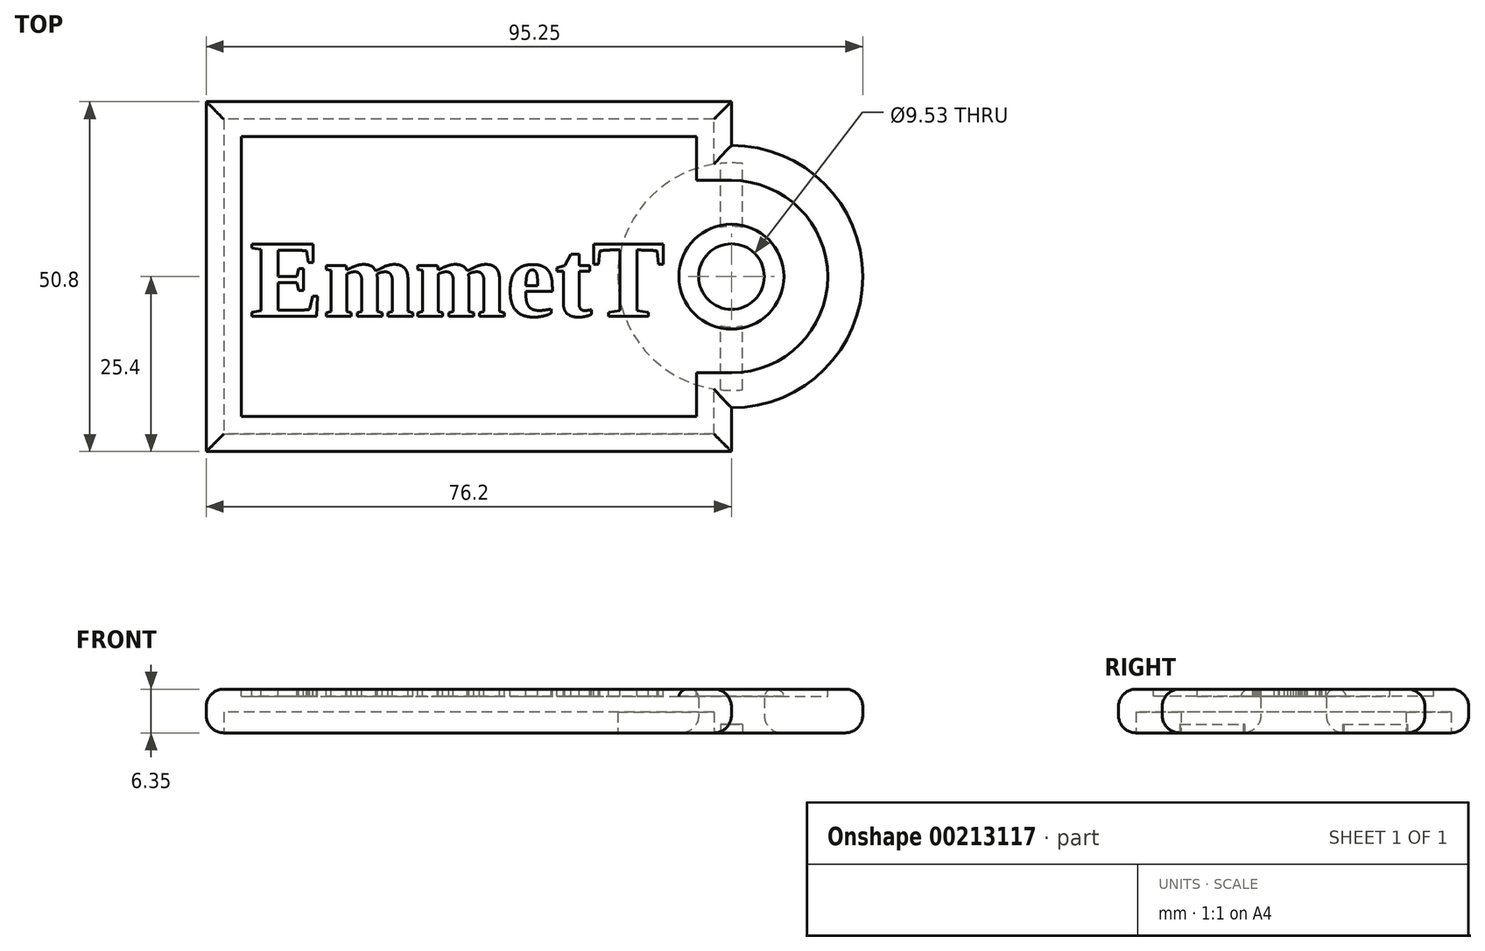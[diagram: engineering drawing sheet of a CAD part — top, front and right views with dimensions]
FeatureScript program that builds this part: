
annotation { "Feature Type Name" : "Feature", "Feature Type Description" : "" }
export const myFeature = defineFeature(function(context is Context, id is Id, definition is map)
    precondition{}
    {
        {
            var Q0;
            Q0=qCreatedBy(makeId("Top.planeOp"),FACE);
            var sketch = newSketch(context, id + "F0", { "sketchPlane" : qUnion([Q0])});
            skLineSegment(sketch, "E0.bottom", {"start": v(0, 0) * mm, "end": v(76.2, 0) * mm});
            skLineSegment(sketch, "E0.top", {"start": v(0, 50.8) * mm, "end": v(76.2, 50.8) * mm});
            skLineSegment(sketch, "E0.left", {"start": v(0, 0) * mm, "end": v(0, 50.8) * mm});
            skLineSegment(sketch, "E0.right", {"start": v(76.2, 0) * mm, "end": v(76.2, 6.35) * mm});
            skArc(sketch, "E1", {"start": v(76.2, 6.35) * mm, "mid": v(95.25, 25.4) * mm, "end": v(76.2, 44.45) * mm});
            skLineSegment(sketch, "E2.trimOffspring", {"start": v(76.2, 44.45) * mm, "end": v(76.2, 50.8) * mm});
            skLineSegment(sketch, "E3", {"start": v(76.2, 44.45) * mm, "end": v(76.2, 6.35) * mm, "construction": true});
            skCircle(sketch, "E4", {"center": v(76.2, 25.4) * mm, "radius": 4.76 * mm});
            skSolve(sketch);
        }
        {
            var Q0;
            Q0 = qSketchRegion(id + "F0", true);
            extrude(context, id + "F1", {"entities" : qUnion([Q0]), "depth" : 6.35 * mm});
        }
        {
            var Q0;
            Q0=makeQuery(id+"F1.opExtrude","CAP_FACE",FACE,{"disambiguationData":[OSD([sQuery(id+"F0.wireOp",EDGE,"E0.bottom"),sQuery(id+"F0.wireOp",EDGE,"E0.top"),sQuery(id+"F0.wireOp",EDGE,"E0.left"),sQuery(id+"F0.wireOp",EDGE,"E0.right"),sQuery(id+"F0.wireOp",EDGE,"E1"),sQuery(id+"F0.wireOp",EDGE,"E2.trimOffspring"),sQuery(id+"F0.wireOp",EDGE,"E4")])],"isStart":true});
            var Q1;
            Q1=makeQuery(id+"F1.opExtrude","CAP_EDGE",EDGE,{"disambiguationData":[OSD([sQuery(id+"F0.wireOp",EDGE,"E0.top")])],"isStart":false});
            var Q2;
            Q2=makeQuery(id+"F1.opExtrude","CAP_EDGE",EDGE,{"disambiguationData":[OSD([sQuery(id+"F0.wireOp",EDGE,"E2.trimOffspring")])],"isStart":false});
            var Q3;
            Q3=makeQuery(id+"F1.opExtrude","CAP_EDGE",EDGE,{"disambiguationData":[OSD([sQuery(id+"F0.wireOp",EDGE,"E1")])],"isStart":false});
            var Q4;
            Q4=makeQuery(id+"F1.opExtrude","CAP_EDGE",EDGE,{"disambiguationData":[OSD([sQuery(id+"F0.wireOp",EDGE,"E0.right")])],"isStart":false});
            var Q5;
            Q5=makeQuery(id+"F1.opExtrude","CAP_EDGE",EDGE,{"disambiguationData":[OSD([sQuery(id+"F0.wireOp",EDGE,"E0.bottom")])],"isStart":false});
            var Q6;
            Q6=makeQuery(id+"F1.opExtrude","CAP_EDGE",EDGE,{"disambiguationData":[OSD([sQuery(id+"F0.wireOp",EDGE,"E0.left")])],"isStart":false});
            var Q7;
            Q7=makeQuery(id+"F1.opExtrude","CAP_EDGE",EDGE,{"disambiguationData":[OSD([sQuery(id+"F0.wireOp",EDGE,"E4")])],"isStart":false});
            fillet(context, id + "F2", {"entities" : qUnion([Q0, Q1, Q2, Q3, Q4, Q5, Q6, Q7]), "radius" : 2.54 * mm, "tangentPropagation" : true, "allowEdgeOverflow" : false});
        }
        {
            var Q0;
            {var subQ0=sQuery(id+"F0.wireOp",EDGE,"E4");var subQ1=sQuery(id+"F0.wireOp",EDGE,"E0.left");var subQ2=sQuery(id+"F0.wireOp",EDGE,"E2.trimOffspring");var subQ3=sQuery(id+"F0.wireOp",EDGE,"E0.bottom");var subQ4=sQuery(id+"F0.wireOp",EDGE,"E0.right");var subQ5=sQuery(id+"F0.wireOp",EDGE,"E0.top");var subQ6=sQuery(id+"F0.wireOp",EDGE,"E1");Q0=makeQuery(id+"F6.boolean.opBoolean","SPLIT",FACE,{"disambiguationData":[TD([makeQuery(id+"F1.opExtrude","SWEPT_FACE",FACE,{"disambiguationData":[OSD([subQ3])]})])],"derivedFrom":makeQuery(id+"F1.opExtrude","CAP_FACE",FACE,{"disambiguationData":[OSD([subQ3,subQ5,subQ1,subQ4,subQ6,subQ2,subQ0])],"isStart":false})});}
            var sketch = newSketch(context, id + "F3", { "sketchPlane" : qUnion([Q0])});
            skLineSegment(sketch, "E5.bottom", {"start": v(5.08, 45.72) * mm, "end": v(71.12, 45.72) * mm});
            skLineSegment(sketch, "E5.top", {"start": v(5.08, 5.08) * mm, "end": v(71.12, 5.08) * mm});
            skLineSegment(sketch, "E5.left", {"start": v(5.08, 45.72) * mm, "end": v(5.08, 5.08) * mm});
            skLineSegment(sketch, "E5.right", {"start": v(71.12, 45.72) * mm, "end": v(71.12, 39.37) * mm});
            skArc(sketch, "E6", {"start": v(76.2, 11.43) * mm, "mid": v(90.17, 25.4) * mm, "end": v(76.2, 39.37) * mm});
            skLineSegment(sketch, "E7", {"start": v(76.2, 11.43) * mm, "end": v(71.12, 11.43) * mm});
            skLineSegment(sketch, "E8", {"start": v(76.2, 39.37) * mm, "end": v(71.12, 39.37) * mm});
            skLineSegment(sketch, "E9.trimOffspring", {"start": v(71.12, 11.43) * mm, "end": v(71.12, 5.08) * mm});
            skSolve(sketch);
        }
        {
            var Q0;
            Q0 = qSketchRegion(id + "F3", true);
            extrude(context, id + "F4", {"entities" : qUnion([Q0]), "operationType" : NewBodyOperationType.REMOVE, "oppositeDirection" : true, "depth" : 1.02 * mm});
        }
        {
            var Q0;
            Q0=makeQuery(id+"F1.opExtrude","CAP_FACE",FACE,{"disambiguationData":[OSD([sQuery(id+"F0.wireOp",EDGE,"E0.bottom"),sQuery(id+"F0.wireOp",EDGE,"E0.top"),sQuery(id+"F0.wireOp",EDGE,"E0.left"),sQuery(id+"F0.wireOp",EDGE,"E0.right"),sQuery(id+"F0.wireOp",EDGE,"E1"),sQuery(id+"F0.wireOp",EDGE,"E2.trimOffspring"),sQuery(id+"F0.wireOp",EDGE,"E4")])],"isStart":false});
            var sketch = newSketch(context, id + "F5", { "sketchPlane" : qUnion([Q0])});
            skText(sketch, "E10", { "text": "EmmetT", "fontName": "Tinos-Bold.ttf"});
            skLineSegment(sketch, "E11", {"start": v(6.35, 25.4) * mm, "end": v(5.08, 25.4) * mm, "construction": true});
            skCircle(sketch, "E12", {"center": v(76.2, 25.4) * mm, "radius": 7.62 * mm});
            skCircle(sketch, "E13", {"center": v(76.2, 25.4) * mm, "radius": 4.76 * mm});
            const initialGuessF5  = {"E10": [0.00635, 0.01966, 1, 0, 0.01148]};
            skSetInitialGuess(sketch, initialGuessF5);
            skSolve(sketch);
        }
        {
            var Q0;
            Q0 = qSketchRegion(id + "F5", true);
            extrude(context, id + "F6", {"entities" : qUnion([Q0]), "operationType" : NewBodyOperationType.ADD, "oppositeDirection" : true, "depth" : 2.54 * mm});
        }
        {
            var Q0;
            Q0=makeQuery(id+"F6.opExtrude","CAP_EDGE",EDGE,{"disambiguationData":[OSD([sQuery(id+"F5.wireOp",EDGE,"E13")])],"isStart":true});
            var Q1;
            Q1=makeQuery(id+"F6.opExtrude","CAP_EDGE",EDGE,{"disambiguationData":[OSD([sQuery(id+"F5.wireOp",EDGE,"E12")])],"isStart":true});
            var Q2;
            Q2=makeQuery(id+"F6.opExtrude","CAP_EDGE",EDGE,{"disambiguationData":[OSD([sQuery(id+"F5.wireOp",EDGE,"E12")])],"isStart":false});
            fillet(context, id + "F7", {"entities" : qUnion([Q0, Q1, Q2]), "radius" : 1.27 * mm, "tangentPropagation" : true, "allowEdgeOverflow" : false});
        }
        {
            var Q0;
            Q0=makeQuery(id+"F1.opExtrude","CAP_FACE",FACE,{"disambiguationData":[OSD([sQuery(id+"F0.wireOp",EDGE,"E0.bottom"),sQuery(id+"F0.wireOp",EDGE,"E0.top"),sQuery(id+"F0.wireOp",EDGE,"E0.left"),sQuery(id+"F0.wireOp",EDGE,"E0.right"),sQuery(id+"F0.wireOp",EDGE,"E1"),sQuery(id+"F0.wireOp",EDGE,"E2.trimOffspring"),sQuery(id+"F0.wireOp",EDGE,"E4")])],"isStart":true});
            var sketch = newSketch(context, id + "F8", { "sketchPlane" : qUnion([Q0])});
            skLineSegment(sketch, "E14.bottom", {"start": v(73.68, -48.26) * mm, "end": v(2.56, -48.26) * mm});
            skLineSegment(sketch, "E14.top", {"start": v(73.68, -2.54) * mm, "end": v(2.56, -2.54) * mm});
            skLineSegment(sketch, "E14.left", {"start": v(73.68, -48.26) * mm, "end": v(73.68, -2.54) * mm, "construction": true});
            skLineSegment(sketch, "E14.right", {"start": v(2.56, -48.26) * mm, "end": v(2.56, -2.54) * mm});
            skLineSegment(sketch, "E15", {"start": v(76.2, -25.4) * mm, "end": v(73.68, -25.4) * mm, "construction": true});
            skArc(sketch, "E16", {"start": v(73.66, -41.71) * mm, "mid": v(59.7, -25.39) * mm, "end": v(73.68, -9.08) * mm});
            skLineSegment(sketch, "E17", {"start": v(73.68, -2.54) * mm, "end": v(73.68, -9.08) * mm});
            skLineSegment(sketch, "E18", {"start": v(73.66, -41.71) * mm, "end": v(73.68, -48.26) * mm});
            skSolve(sketch);
        }
        {
            var Q0;
            Q0 = qSketchRegion(id + "F8", true);
            extrude(context, id + "F9", {"entities" : qUnion([Q0]), "operationType" : NewBodyOperationType.REMOVE, "oppositeDirection" : true, "depth" : 3.02 * mm});
        }
        {
            var Q0;
            {var subQ0=sQuery(id+"F0.wireOp",EDGE,"E4");var subQ1=sQuery(id+"F0.wireOp",EDGE,"E2.trimOffspring");var subQ2=sQuery(id+"F0.wireOp",EDGE,"E1");var subQ3=sQuery(id+"F0.wireOp",EDGE,"E0.right");Q0=makeQuery(id+"F9.boolean.opBoolean","SPLIT",FACE,{"disambiguationData":[TD([makeQuery(id+"F9.opExtrude","SWEPT_FACE",FACE,{"disambiguationData":[OSD([sQuery(id+"F8.wireOp",EDGE,"E16")])]})])],"derivedFrom":makeQuery(id+"F1.opExtrude","CAP_FACE",FACE,{"disambiguationData":[OSD([sQuery(id+"F0.wireOp",EDGE,"E0.bottom"),sQuery(id+"F0.wireOp",EDGE,"E0.top"),sQuery(id+"F0.wireOp",EDGE,"E0.left"),subQ3,subQ2,subQ1,subQ0])],"isStart":true})});}
            var sketch = newSketch(context, id + "F10", { "sketchPlane" : qUnion([Q0])});
            skLineSegment(sketch, "E19.bottom", {"start": v(74.61, -8.97) * mm, "end": v(77.79, -8.97) * mm});
            skLineSegment(sketch, "E19.top", {"start": v(74.61, -41.83) * mm, "end": v(77.79, -41.83) * mm});
            skLineSegment(sketch, "E19.left", {"start": v(74.61, -8.97) * mm, "end": v(74.61, -18.27) * mm});
            skLineSegment(sketch, "E19.right", {"start": v(77.79, -8.97) * mm, "end": v(77.79, -18.27) * mm});
            skPoint(sketch, "E19.middle", {"position": v(76.2, -25.4) * mm});
            skArc(sketch, "E20", {"start": v(77.79, -41.83) * mm, "mid": v(76.2, -41.91) * mm, "end": v(74.61, -41.83) * mm});
            skArc(sketch, "E21", {"start": v(74.61, -8.97) * mm, "mid": v(76.2, -8.89) * mm, "end": v(77.79, -8.97) * mm});
            skArc(sketch, "E22", {"start": v(74.61, -18.27) * mm, "mid": v(76.2, -18.1) * mm, "end": v(77.79, -18.27) * mm});
            skArc(sketch, "E23", {"start": v(77.79, -32.53) * mm, "mid": v(76.2, -32.7) * mm, "end": v(74.61, -32.53) * mm});
            skLineSegment(sketch, "E24.trimOffspring", {"start": v(74.61, -32.53) * mm, "end": v(74.61, -41.83) * mm});
            skLineSegment(sketch, "E25.trimOffspring", {"start": v(77.79, -32.53) * mm, "end": v(77.79, -41.83) * mm});
            skSolve(sketch);
        }
        {
            var Q0;
            Q0 = qSketchRegion(id + "F10", true);
            extrude(context, id + "F11", {"entities" : qUnion([Q0]), "operationType" : NewBodyOperationType.REMOVE, "oppositeDirection" : true, "depth" : 1.27 * mm});
        }
        {
            var Q0;
            {var subQ0=sQuery(id+"F0.wireOp",EDGE,"E1");var subQ2=sQuery(id+"F0.wireOp",EDGE,"E4");var subQ4=sQuery(id+"F0.wireOp",EDGE,"E2.trimOffspring");var subQ5=sQuery(id+"F0.wireOp",EDGE,"E0.right");Q0=makeQuery(id+"F11.boolean.opBoolean","SPLIT",FACE,{"disambiguationData":[TD([makeQuery(id+"F11.opExtrude","SWEPT_FACE",FACE,{"disambiguationData":[OSD([sQuery(id+"F10.wireOp",EDGE,"E19.right")])]})])],"derivedFrom":makeQuery(id+"F9.boolean.opBoolean","SPLIT",FACE,{"disambiguationData":[TD([makeQuery(id+"F9.opExtrude","SWEPT_FACE",FACE,{"disambiguationData":[OSD([sQuery(id+"F8.wireOp",EDGE,"E16")])]})])],"derivedFrom":makeQuery(id+"F1.opExtrude","CAP_FACE",FACE,{"disambiguationData":[OSD([sQuery(id+"F0.wireOp",EDGE,"E0.bottom"),sQuery(id+"F0.wireOp",EDGE,"E0.top"),sQuery(id+"F0.wireOp",EDGE,"E0.left"),subQ5,subQ0,subQ4,subQ2])],"isStart":true})})});}
            var sketch = newSketch(context, id + "F12", { "sketchPlane" : qUnion([Q0])});
            skArc(sketch, "E26", {"start": v(77.79, -41.83) * mm, "mid": v(92.7, -25.4) * mm, "end": v(77.79, -8.97) * mm});
            skArc(sketch, "E27", {"start": v(77.79, -32.53) * mm, "mid": v(83.5, -25.4) * mm, "end": v(77.79, -18.27) * mm});
            skLineSegment(sketch, "E28", {"start": v(77.79, -41.83) * mm, "end": v(77.79, -32.53) * mm});
            skLineSegment(sketch, "E29", {"start": v(77.79, -18.27) * mm, "end": v(77.79, -8.97) * mm});
            skSolve(sketch);
        }
        {
            var Q0;
            Q0 = qSketchRegion(id + "F12", true);
            extrude(context, id + "F13", {"entities" : qUnion([Q0]), "operationType" : NewBodyOperationType.REMOVE, "depth" : 0.5 * mm});
        }
    });
